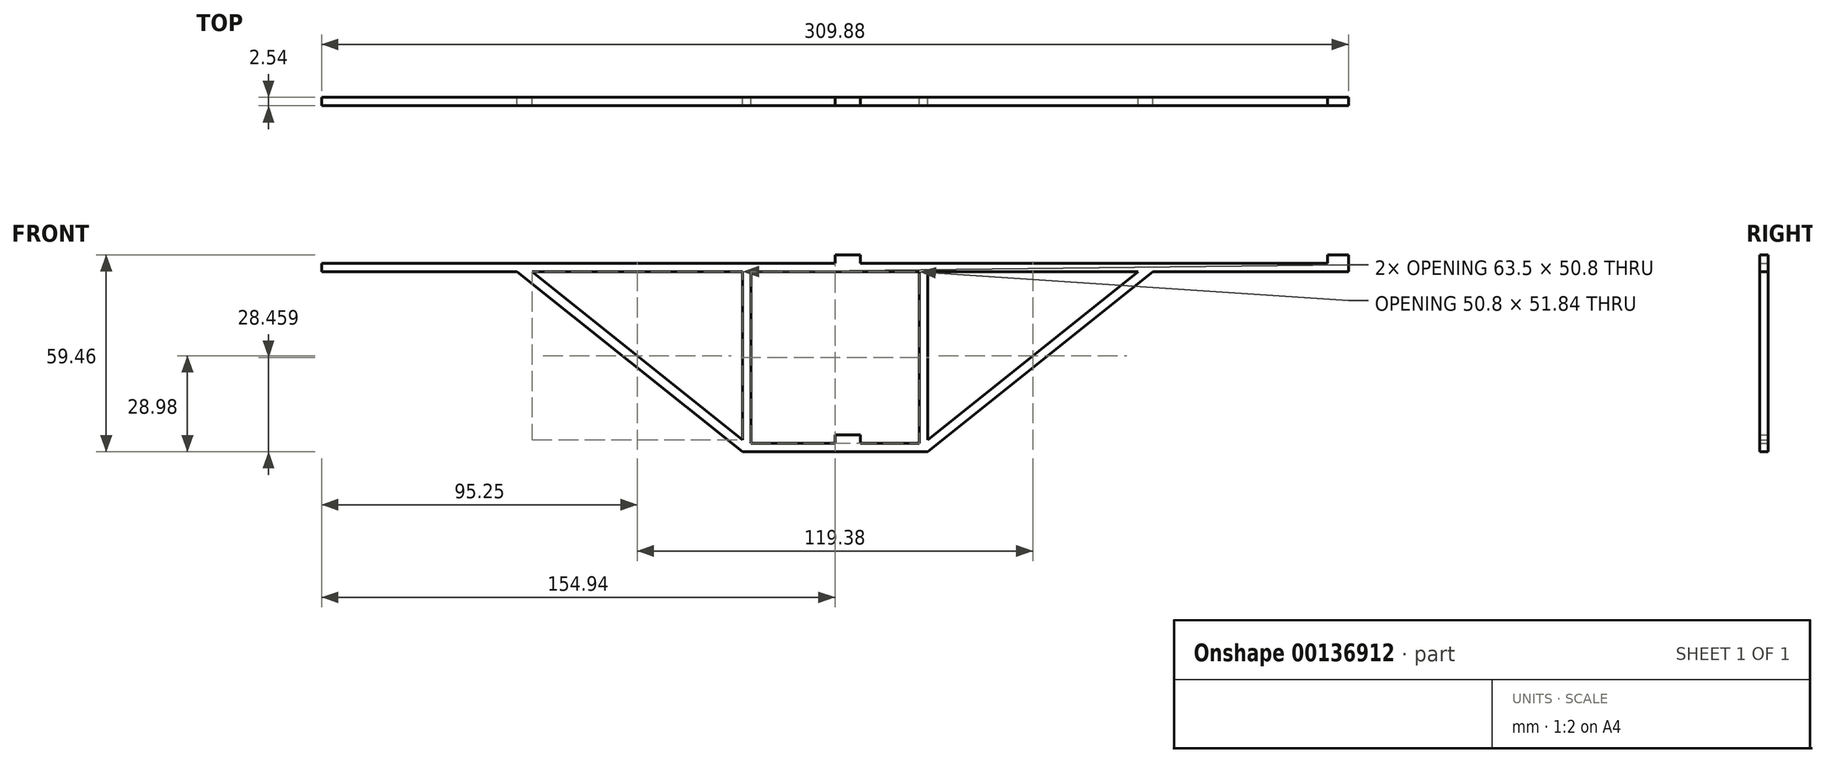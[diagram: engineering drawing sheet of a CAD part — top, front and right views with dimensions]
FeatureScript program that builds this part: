
annotation { "Feature Type Name" : "Feature", "Feature Type Description" : "" }
export const myFeature = defineFeature(function(context is Context, id is Id, definition is map)
    precondition{}
    {
        {
            var Q0;
            Q0=qCreatedBy(makeId("Front.planeOp"),FACE);
            var sketch = newSketch(context, id + "F0", { "sketchPlane" : qUnion([Q0])});
            skLineSegment(sketch, "E0.bottom", {"start": v(-127, 0) * mm, "end": v(0, 0) * mm});
            skLineSegment(sketch, "E0.top", {"start": v(-127, 2.54) * mm, "end": v(0, 2.54) * mm});
            skLineSegment(sketch, "E0.left", {"start": v(-127, 0) * mm, "end": v(-127, 2.54) * mm});
            skLineSegment(sketch, "E0.right", {"start": v(0, 0) * mm, "end": v(0, 2.54) * mm});
            skLineSegment(sketch, "E1", {"start": v(-63.5, 0) * mm, "end": v(0, -50.8) * mm});
            skLineSegment(sketch, "E2", {"start": v(0, -50.8) * mm, "end": v(0, -54.38) * mm});
            skLineSegment(sketch, "E3", {"start": v(0, -54.38) * mm, "end": v(-67.98, 0) * mm});
            skLineSegment(sketch, "E4", {"start": v(-67.98, 0) * mm, "end": v(-63.5, 0) * mm});
            skLineSegment(sketch, "E5.bottom", {"start": v(0, 2.54) * mm, "end": v(2.54, 2.54) * mm});
            skLineSegment(sketch, "E5.top", {"start": v(0, -54.38) * mm, "end": v(2.54, -54.38) * mm});
            skLineSegment(sketch, "E5.left", {"start": v(0, 2.54) * mm, "end": v(0, -54.38) * mm});
            skLineSegment(sketch, "E5.right", {"start": v(2.54, 2.54) * mm, "end": v(2.54, -54.38) * mm});
            skLineSegment(sketch, "E6.bottom", {"start": v(2.54, 2.54) * mm, "end": v(27.94, 2.54) * mm});
            skLineSegment(sketch, "E6.top", {"start": v(2.54, 0) * mm, "end": v(27.94, 0) * mm});
            skLineSegment(sketch, "E6.left", {"start": v(2.54, 2.54) * mm, "end": v(2.54, 0) * mm});
            skLineSegment(sketch, "E6.right", {"start": v(27.94, 2.54) * mm, "end": v(27.94, 0) * mm});
            skLineSegment(sketch, "E7.bottom", {"start": v(2.54, -54.38) * mm, "end": v(27.94, -54.38) * mm});
            skLineSegment(sketch, "E7.top", {"start": v(2.54, -51.84) * mm, "end": v(27.94, -51.84) * mm});
            skLineSegment(sketch, "E7.left", {"start": v(2.54, -54.38) * mm, "end": v(2.54, -51.84) * mm});
            skLineSegment(sketch, "E7.right", {"start": v(27.94, -54.38) * mm, "end": v(27.94, -51.84) * mm});
            skLineSegment(sketch, "E8.MirrorCS", {"start": v(55.88, -50.8) * mm, "end": v(55.88, -54.38) * mm});
            skLineSegment(sketch, "E9.MirrorCS", {"start": v(55.88, -54.38) * mm, "end": v(53.34, -54.38) * mm});
            skLineSegment(sketch, "E10.MirrorCS", {"start": v(55.88, 0) * mm, "end": v(55.88, 2.54) * mm});
            skLineSegment(sketch, "E11.MirrorCS", {"start": v(53.34, 2.54) * mm, "end": v(53.34, 0) * mm});
            skLineSegment(sketch, "E12.MirrorCS", {"start": v(55.88, 2.54) * mm, "end": v(53.34, 2.54) * mm});
            skLineSegment(sketch, "E13.MirrorCS", {"start": v(53.34, -54.38) * mm, "end": v(53.34, -51.84) * mm});
            skLineSegment(sketch, "E14.MirrorCS", {"start": v(123.86, 0) * mm, "end": v(119.38, 0) * mm});
            skLineSegment(sketch, "E15.MirrorCS", {"start": v(182.88, 0) * mm, "end": v(182.88, 2.54) * mm});
            skLineSegment(sketch, "E16.MirrorCS", {"start": v(119.38, 0) * mm, "end": v(55.88, -50.8) * mm});
            skLineSegment(sketch, "E17.MirrorCS", {"start": v(53.34, 0) * mm, "end": v(27.94, 0) * mm});
            skLineSegment(sketch, "E18.MirrorCS", {"start": v(53.34, 2.54) * mm, "end": v(53.34, -54.38) * mm});
            skLineSegment(sketch, "E19.MirrorCS", {"start": v(53.34, -51.84) * mm, "end": v(27.94, -51.84) * mm});
            skLineSegment(sketch, "E20.MirrorCS", {"start": v(182.88, 0) * mm, "end": v(55.88, 0) * mm});
            skLineSegment(sketch, "E21.MirrorCS", {"start": v(55.88, -54.38) * mm, "end": v(123.86, 0) * mm});
            skLineSegment(sketch, "E22.MirrorCS", {"start": v(53.34, -54.38) * mm, "end": v(27.94, -54.38) * mm});
            skLineSegment(sketch, "E23.MirrorCS", {"start": v(182.88, 2.54) * mm, "end": v(55.88, 2.54) * mm});
            skLineSegment(sketch, "E24.MirrorCS", {"start": v(53.34, 2.54) * mm, "end": v(27.94, 2.54) * mm});
            skLineSegment(sketch, "E25.MirrorCS", {"start": v(55.88, 2.54) * mm, "end": v(55.88, -54.38) * mm});
            skLineSegment(sketch, "E26.bottom", {"start": v(-127, 2.54) * mm, "end": v(-120.65, 2.54) * mm});
            skLineSegment(sketch, "E26.top", {"start": v(-127, 5.08) * mm, "end": v(-120.65, 5.08) * mm});
            skLineSegment(sketch, "E26.left", {"start": v(-127, 2.54) * mm, "end": v(-127, 5.08) * mm});
            skLineSegment(sketch, "E26.right", {"start": v(-120.65, 2.54) * mm, "end": v(-120.65, 5.08) * mm});
            skLineSegment(sketch, "E27.MirrorCS", {"start": v(176.53, 2.54) * mm, "end": v(176.53, 5.08) * mm});
            skLineSegment(sketch, "E28.MirrorCS", {"start": v(182.88, 2.54) * mm, "end": v(176.53, 2.54) * mm});
            skLineSegment(sketch, "E29.MirrorCS", {"start": v(182.88, 5.08) * mm, "end": v(176.53, 5.08) * mm});
            skLineSegment(sketch, "E30.MirrorCS", {"start": v(182.88, 2.54) * mm, "end": v(182.88, 5.08) * mm});
            skLineSegment(sketch, "E31.bottom", {"start": v(27.94, -51.84) * mm, "end": v(20.32, -51.84) * mm});
            skLineSegment(sketch, "E31.top", {"start": v(27.94, -49.3) * mm, "end": v(20.32, -49.3) * mm});
            skLineSegment(sketch, "E31.left", {"start": v(27.94, -51.84) * mm, "end": v(27.94, -49.3) * mm});
            skLineSegment(sketch, "E31.right", {"start": v(20.32, -51.84) * mm, "end": v(20.32, -49.3) * mm});
            skLineSegment(sketch, "E32.MirrorCS", {"start": v(35.56, -51.84) * mm, "end": v(35.56, -49.3) * mm});
            skLineSegment(sketch, "E33.MirrorCS", {"start": v(27.94, -51.84) * mm, "end": v(35.56, -51.84) * mm});
            skLineSegment(sketch, "E34.MirrorCS", {"start": v(27.94, -49.3) * mm, "end": v(35.56, -49.3) * mm});
            skLineSegment(sketch, "E35.bottom", {"start": v(27.94, 2.54) * mm, "end": v(20.32, 2.54) * mm});
            skLineSegment(sketch, "E35.top", {"start": v(27.94, 5.08) * mm, "end": v(20.32, 5.08) * mm});
            skLineSegment(sketch, "E35.left", {"start": v(27.94, 2.54) * mm, "end": v(27.94, 5.08) * mm});
            skLineSegment(sketch, "E35.right", {"start": v(20.32, 2.54) * mm, "end": v(20.32, 5.08) * mm});
            skLineSegment(sketch, "E36.MirrorCS", {"start": v(35.56, 2.54) * mm, "end": v(35.56, 5.08) * mm});
            skLineSegment(sketch, "E37.MirrorCS", {"start": v(27.94, 5.08) * mm, "end": v(35.56, 5.08) * mm});
            skLineSegment(sketch, "E38.MirrorCS", {"start": v(27.94, 2.54) * mm, "end": v(35.56, 2.54) * mm});
            skSolve(sketch);
        }
        {
            var Q0;
            {var subQ1=sQuery(id+"F0.wireOp",EDGE,"E0.top");Q0=makeQuery(id+"F0.imprint","IMPRINT",FACE,{"disambiguationData":[TD([[makeQuery(id+"F0.imprint","IMPRINT",EDGE,{"derivedFrom":subQ1}),-1.0]])]});}
            var Q1;
            {var subQ0=sQuery(id+"F0.wireOp",EDGE,"E1");Q1=makeQuery(id+"F0.imprint","IMPRINT",FACE,{"disambiguationData":[TD([[makeQuery(id+"F0.imprint","IMPRINT",EDGE,{"derivedFrom":subQ0}),-1.0]])]});}
            var Q2;
            Q2=makeQuery(id+"F0.imprint","IMPRINT",FACE,{"disambiguationData":[TD([[makeQuery(id+"F0.imprint","IMPRINT",EDGE,{"derivedFrom":sQuery(id+"F0.wireOp",EDGE,"E6.bottom")}),-1.0]])]});
            var Q3;
            {var subQ3=sQuery(id+"F0.wireOp",EDGE,"E5.bottom");Q3=makeQuery(id+"F0.imprint","IMPRINT",FACE,{"disambiguationData":[TD([[makeQuery(id+"F0.imprint","IMPRINT",EDGE,{"derivedFrom":subQ3}),-1.0]])]});}
            var Q4;
            Q4=makeQuery(id+"F0.imprint","IMPRINT",FACE,{"disambiguationData":[TD([[makeQuery(id+"F0.imprint","IMPRINT",EDGE,{"derivedFrom":sQuery(id+"F0.wireOp",EDGE,"E7.bottom")}),1.0]])]});
            var Q5;
            Q5=makeQuery(id+"F0.imprint","IMPRINT",FACE,{"disambiguationData":[TD([[makeQuery(id+"F0.imprint","IMPRINT",EDGE,{"derivedFrom":sQuery(id+"F0.wireOp",EDGE,"E7.right")}),-1.0]])]});
            var Q6;
            {var subQ3=sQuery(id+"F0.wireOp",EDGE,"E9.MirrorCS");Q6=makeQuery(id+"F0.imprint","IMPRINT",FACE,{"disambiguationData":[TD([[makeQuery(id+"F0.imprint","IMPRINT",EDGE,{"derivedFrom":subQ3}),-1.0]])]});}
            var Q7;
            Q7=makeQuery(id+"F0.imprint","IMPRINT",FACE,{"disambiguationData":[TD([[makeQuery(id+"F0.imprint","IMPRINT",EDGE,{"derivedFrom":sQuery(id+"F0.wireOp",EDGE,"E6.right")}),1.0]])]});
            var Q8;
            {var subQ6=sQuery(id+"F0.wireOp",EDGE,"E15.MirrorCS");Q8=makeQuery(id+"F0.imprint","IMPRINT",FACE,{"disambiguationData":[TD([[makeQuery(id+"F0.imprint","IMPRINT",EDGE,{"derivedFrom":subQ6}),1.0]])]});}
            var Q9;
            {var subQ0=sQuery(id+"F0.wireOp",EDGE,"E16.MirrorCS");Q9=makeQuery(id+"F0.imprint","IMPRINT",FACE,{"disambiguationData":[TD([[makeQuery(id+"F0.imprint","IMPRINT",EDGE,{"derivedFrom":subQ0}),1.0]])]});}
            extrude(context, id + "F1", {"entities" : qUnion([Q0, Q1, Q2, Q3, Q4, Q5, Q6, Q7, Q8, Q9]), "depth" : 2.54 * mm});
        }
        {
            var Q0;
            Q0=makeQuery(id+"F0.imprint","IMPRINT",FACE,{"disambiguationData":[TD([[makeQuery(id+"F0.imprint","IMPRINT",EDGE,{"derivedFrom":sQuery(id+"F0.wireOp",EDGE,"E26.bottom")}),1.0]])]});
            var Q1;
            Q1=makeQuery(id+"F0.imprint","IMPRINT",FACE,{"disambiguationData":[TD([[makeQuery(id+"F0.imprint","IMPRINT",EDGE,{"derivedFrom":sQuery(id+"F0.wireOp",EDGE,"E35.bottom")}),-1.0]])]});
            var Q2;
            Q2=makeQuery(id+"F0.imprint","IMPRINT",FACE,{"disambiguationData":[TD([[makeQuery(id+"F0.imprint","IMPRINT",EDGE,{"derivedFrom":sQuery(id+"F0.wireOp",EDGE,"E35.left")}),-1.0]])]});
            var Q3;
            Q3=makeQuery(id+"F0.imprint","IMPRINT",FACE,{"disambiguationData":[TD([[makeQuery(id+"F0.imprint","IMPRINT",EDGE,{"derivedFrom":sQuery(id+"F0.wireOp",EDGE,"E27.MirrorCS")}),-1.0]])]});
            var Q4;
            Q4=makeQuery(id+"F0.imprint","IMPRINT",FACE,{"disambiguationData":[TD([[makeQuery(id+"F0.imprint","IMPRINT",EDGE,{"derivedFrom":sQuery(id+"F0.wireOp",EDGE,"E31.bottom")}),-1.0]])]});
            var Q5;
            Q5=makeQuery(id+"F0.imprint","IMPRINT",FACE,{"disambiguationData":[TD([[makeQuery(id+"F0.imprint","IMPRINT",EDGE,{"derivedFrom":sQuery(id+"F0.wireOp",EDGE,"E31.left")}),-1.0]])]});
            extrude(context, id + "F2", {"entities" : qUnion([Q0, Q1, Q2, Q3, Q4, Q5]), "operationType" : NewBodyOperationType.ADD, "depth" : 2.54 * mm});
        }
    });
